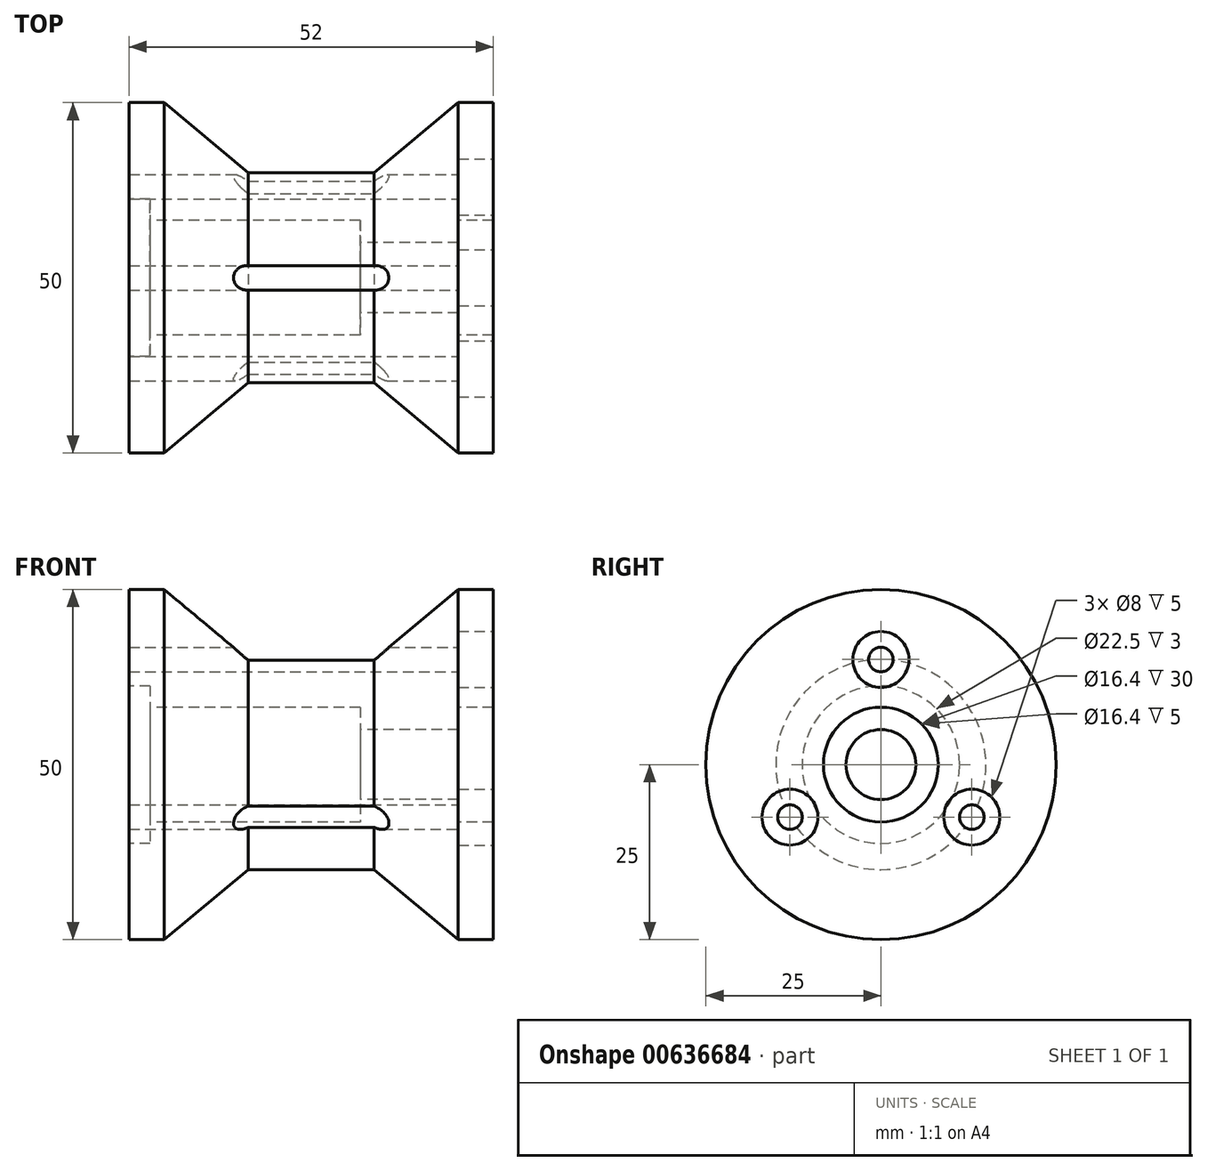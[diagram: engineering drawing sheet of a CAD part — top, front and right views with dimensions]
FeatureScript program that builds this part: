
annotation { "Feature Type Name" : "Feature", "Feature Type Description" : "" }
export const myFeature = defineFeature(function(context is Context, id is Id, definition is map)
    precondition{}
    {
        {
            var Q0;
            Q0=qCreatedBy(makeId("Front.planeOp"),FACE);
            var sketch = newSketch(context, id + "F0", { "sketchPlane" : qUnion([Q0])});
            skLineSegment(sketch, "E0", {"start": v(-107.3, 0) * mm, "end": v(120.58, 0) * mm, "construction": true});
            skLineSegment(sketch, "E1", {"start": v(-12.38, 25) * mm, "end": v(-12.38, 8.2) * mm});
            skLineSegment(sketch, "E2", {"start": v(-64.38, 25) * mm, "end": v(-64.38, 11.25) * mm});
            skLineSegment(sketch, "E3", {"start": v(-64.38, 11.25) * mm, "end": v(-61.38, 11.25) * mm});
            skLineSegment(sketch, "E4", {"start": v(-61.38, 8.2) * mm, "end": v(-31.38, 8.2) * mm});
            skLineSegment(sketch, "E5", {"start": v(-31.38, 8.2) * mm, "end": v(-31.38, 5) * mm});
            skLineSegment(sketch, "E6", {"start": v(-31.38, 5) * mm, "end": v(-17.38, 5) * mm});
            skLineSegment(sketch, "E7", {"start": v(-17.38, 5) * mm, "end": v(-17.38, 8.2) * mm});
            skLineSegment(sketch, "E8", {"start": v(-17.38, 8.2) * mm, "end": v(-12.38, 8.2) * mm});
            skLineSegment(sketch, "E9", {"start": v(-61.38, 11.25) * mm, "end": v(-61.38, 8.2) * mm});
            skLineSegment(sketch, "E10", {"start": v(-17.38, 25) * mm, "end": v(-29.38, 15) * mm});
            skLineSegment(sketch, "E11", {"start": v(-29.38, 15) * mm, "end": v(-47.38, 15) * mm});
            skLineSegment(sketch, "E12", {"start": v(-47.38, 15) * mm, "end": v(-59.38, 25) * mm});
            skLineSegment(sketch, "E13", {"start": v(-64.38, 25) * mm, "end": v(-59.38, 25) * mm});
            skLineSegment(sketch, "E14", {"start": v(-17.38, 25) * mm, "end": v(-12.38, 25) * mm});
            skSolve(sketch);
        }
        {
            var Q0;
            Q0 = qSketchRegion(id + "F0", true);
            var Q1;
            Q1=sQuery(id+"F0.wireOp",EDGE,"E0");
            revolve(context, id + "F1", {"entities" : qUnion([Q0]), "axis" : qUnion([Q1]), "revolveType" : RevolveType.FULL});
        }
        {
            var Q0;
            Q0=qCreatedBy(makeId("Right.planeOp"),FACE);
            var sketch = newSketch(context, id + "F2", { "sketchPlane" : qUnion([Q0])});
            skPoint(sketch, "E15", {"position": v(0, 15) * mm});
            skPoint(sketch, "E16.1.0", {"position": v(-13, -7.5) * mm});
            skPoint(sketch, "E16.2.0", {"position": v(13, -7.5) * mm});
            skPoint(sketch, "E16.center", {"position": v(0, 0) * mm});
            skSolve(sketch);
        }
        {
            var Q0;
            Q0=sQuery(id+"F2.wireOp",VERTEX,"E15");
            var Q1;
            Q1=sQuery(id+"F2.wireOp",VERTEX,"E16.1.0");
            var Q2;
            Q2=sQuery(id+"F2.wireOp",VERTEX,"E16.2.0");
            var Q3;
            Q3=makeQuery(id+"F1.opRevolve","SWEPT_BODY",BODY,{"disambiguationData":[OSD([sQuery(id+"F0.wireOp",EDGE,"E1"),sQuery(id+"F0.wireOp",EDGE,"E2"),sQuery(id+"F0.wireOp",EDGE,"E3"),sQuery(id+"F0.wireOp",EDGE,"E4"),sQuery(id+"F0.wireOp",EDGE,"E5"),sQuery(id+"F0.wireOp",EDGE,"E6"),sQuery(id+"F0.wireOp",EDGE,"l6izbEps-1ZdT-1aI4-9VYW-BdPGSueKKqRx"),sQuery(id+"F0.wireOp",EDGE,"E7"),sQuery(id+"F0.wireOp",EDGE,"E8"),sQuery(id+"F0.wireOp",EDGE,"E9")])]});
            hole(context, id + "F3", {"style" : HoleStyle.C_BORE, "endStyle" : HoleEndStyle.THROUGH, "holeDiameter" : 3.5 * mm, "cBoreDiameter" : 8 * mm, "cBoreDepth" : 5 * mm, "majorDiameter" : 5 * mm, "isTappedThrough" : true, "tappedDepth" : 12 * mm, "tapClearance" : 3, "locations" : qUnion([Q0, Q1, Q2]), "scope" : qUnion([Q3])});
        }
    });
